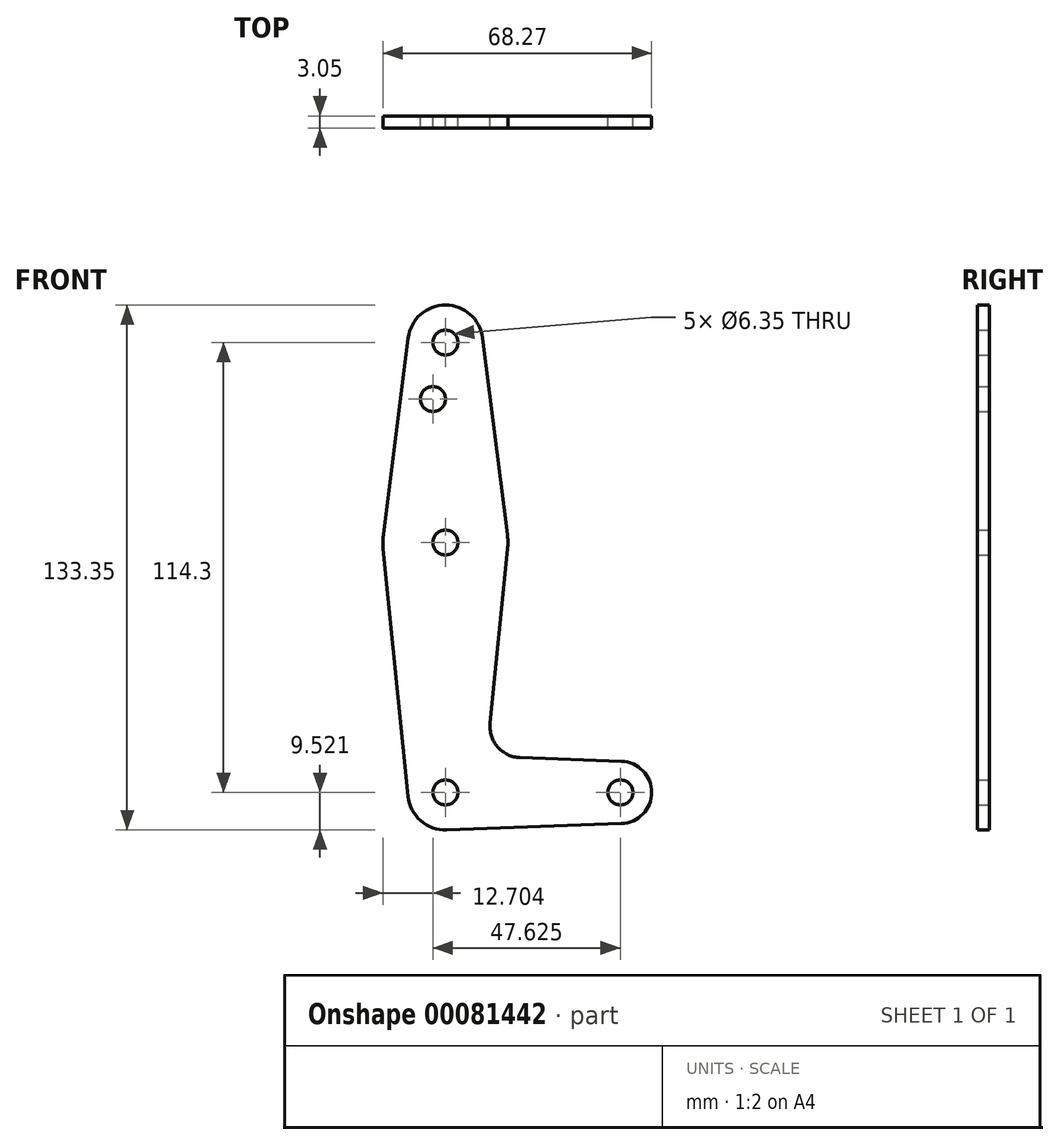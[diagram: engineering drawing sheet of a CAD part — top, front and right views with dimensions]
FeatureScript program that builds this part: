
annotation { "Feature Type Name" : "Feature", "Feature Type Description" : "" }
export const myFeature = defineFeature(function(context is Context, id is Id, definition is map)
    precondition{}
    {
        {
            var Q0;
            Q0=qCreatedBy(makeId("Front.planeOp"),FACE);
            var sketch = newSketch(context, id + "F0", { "sketchPlane" : qUnion([Q0])});
            skLineSegment(sketch, "E0", {"start": v(-53.94, 50.88) * mm, "end": v(-53.94, -63.42) * mm, "construction": true});
            skLineSegment(sketch, "E1", {"start": v(-53.94, -63.42) * mm, "end": v(-9.5, -63.42) * mm, "construction": true});
            skCircle(sketch, "E2", {"center": v(-53.94, 50.88) * mm, "radius": 9.53 * mm});
            skCircle(sketch, "E3", {"center": v(-53.94, 0.08) * mm, "radius": 15.88 * mm});
            skCircle(sketch, "E4", {"center": v(-53.94, -63.42) * mm, "radius": 9.52 * mm});
            skCircle(sketch, "E5", {"center": v(-9.5, -63.42) * mm, "radius": 7.94 * mm});
            skLineSegment(sketch, "E6", {"start": v(-63.4, 52.07) * mm, "end": v(-69.7, 2.07) * mm});
            skLineSegment(sketch, "E7", {"start": v(-44.5, 52.07) * mm, "end": v(-38.2, 2.07) * mm});
            skLineSegment(sketch, "E8", {"start": v(-38.15, -1.5) * mm, "end": v(-42.6, -45.83) * mm});
            skLineSegment(sketch, "E9", {"start": v(-69.74, -1.5) * mm, "end": v(-63.42, -64.37) * mm});
            skLineSegment(sketch, "E10", {"start": v(-53.6, -72.94) * mm, "end": v(-9.2, -71.35) * mm});
            skLineSegment(sketch, "E11", {"start": v(-9.2, -55.49) * mm, "end": v(-34.97, -54.57) * mm});
            skCircle(sketch, "E12", {"center": v(-53.94, 50.88) * mm, "radius": 3.18 * mm});
            skCircle(sketch, "E13", {"center": v(-53.94, 0.08) * mm, "radius": 3.18 * mm});
            skCircle(sketch, "E14", {"center": v(-53.94, -63.42) * mm, "radius": 3.18 * mm});
            skCircle(sketch, "E15", {"center": v(-9.5, -63.42) * mm, "radius": 3.18 * mm});
            skCircle(sketch, "E16", {"center": v(-57.12, 36.53) * mm, "radius": 3.18 * mm});
            skArc(sketch, "E17.filletArc", {"start": v(-42.6, -45.83) * mm, "mid": v(-40.68, -51.85) * mm, "end": v(-34.97, -54.57) * mm});
            skSolve(sketch);
        }
        {
            var Q0;
            Q0 = qSketchRegion(id + "F0", true);
            extrude(context, id + "F1", {"entities" : qUnion([Q0]), "depth" : 3.05 * mm});
        }
    });
